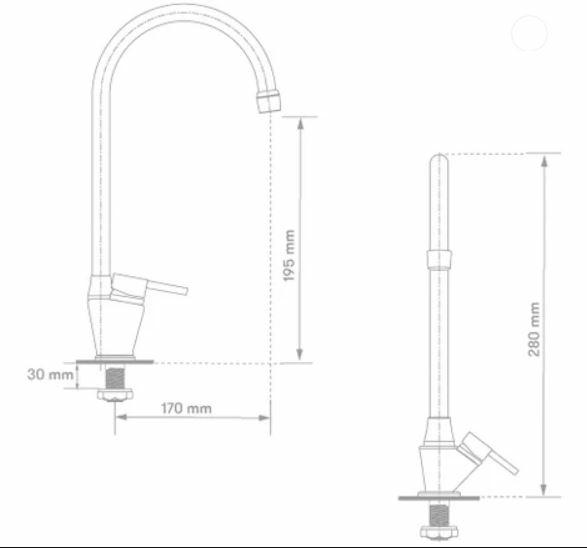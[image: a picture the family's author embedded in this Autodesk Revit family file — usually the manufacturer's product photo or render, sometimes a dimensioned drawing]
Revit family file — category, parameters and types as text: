
# Revit family: 01-2115-11 MEZCLADOR LAVAPLATOS MONOMANDO COLECCIÓN VIVALDI
name_source: partatom
category: Plumbing Fixtures
revit_build: Autodesk Revit 2018 (Build: 20170223_1515(x64)
units: mm (PartAtom-declared; Revit-internal decimal feet)

## family parameters
Cut with Voids When Loaded = No
Host = Face
OmniClass Number = 23.31.11.00
Part Type = Normal
Room Calculation Point = No
Round Connector Dimension = Use Diameter
Shared = No

## types (1)
- 01-2115-11
    Alto aireador = 195 mm
    Alto brazo = 280 mm
    Ancho brazo = 170 mm  [stored 0.557743 ft]
    Brazo = Metal - Acero inoxidable Cromado
    CW Connection = Yes
    Cuerpo y Aireador = Metal Laton Cromado
    Default Elevation = 0 mm  [stored 0 ft]
    Description = MONOMANDO
    HW Connection = Yes
    Link Ficha Tecnica = http://infotecnica.gricol.com
    Manija = Metal Zamak Cromado
    Manufacturer = Gricol
    Model = 01-2115-11
    Product Name = MEZCLADOR LAVAPLATOS MONOMANDO COLECCIÓN VIVALDI
    Tuerca brazo = Plastico - ABS Cromado
    Type Image = <None>
    URL = https://www.gricol.com
    Vent Connection = No
    Waste Connection = No

note: [stored X ft] marks values corroborated as IEEE doubles in the binary element streams (Revit-internal decimal feet)

## geometry (parser evidence)
native form markers: Blend x2, Sweep x6
no freeform markers — native parametric forms only
